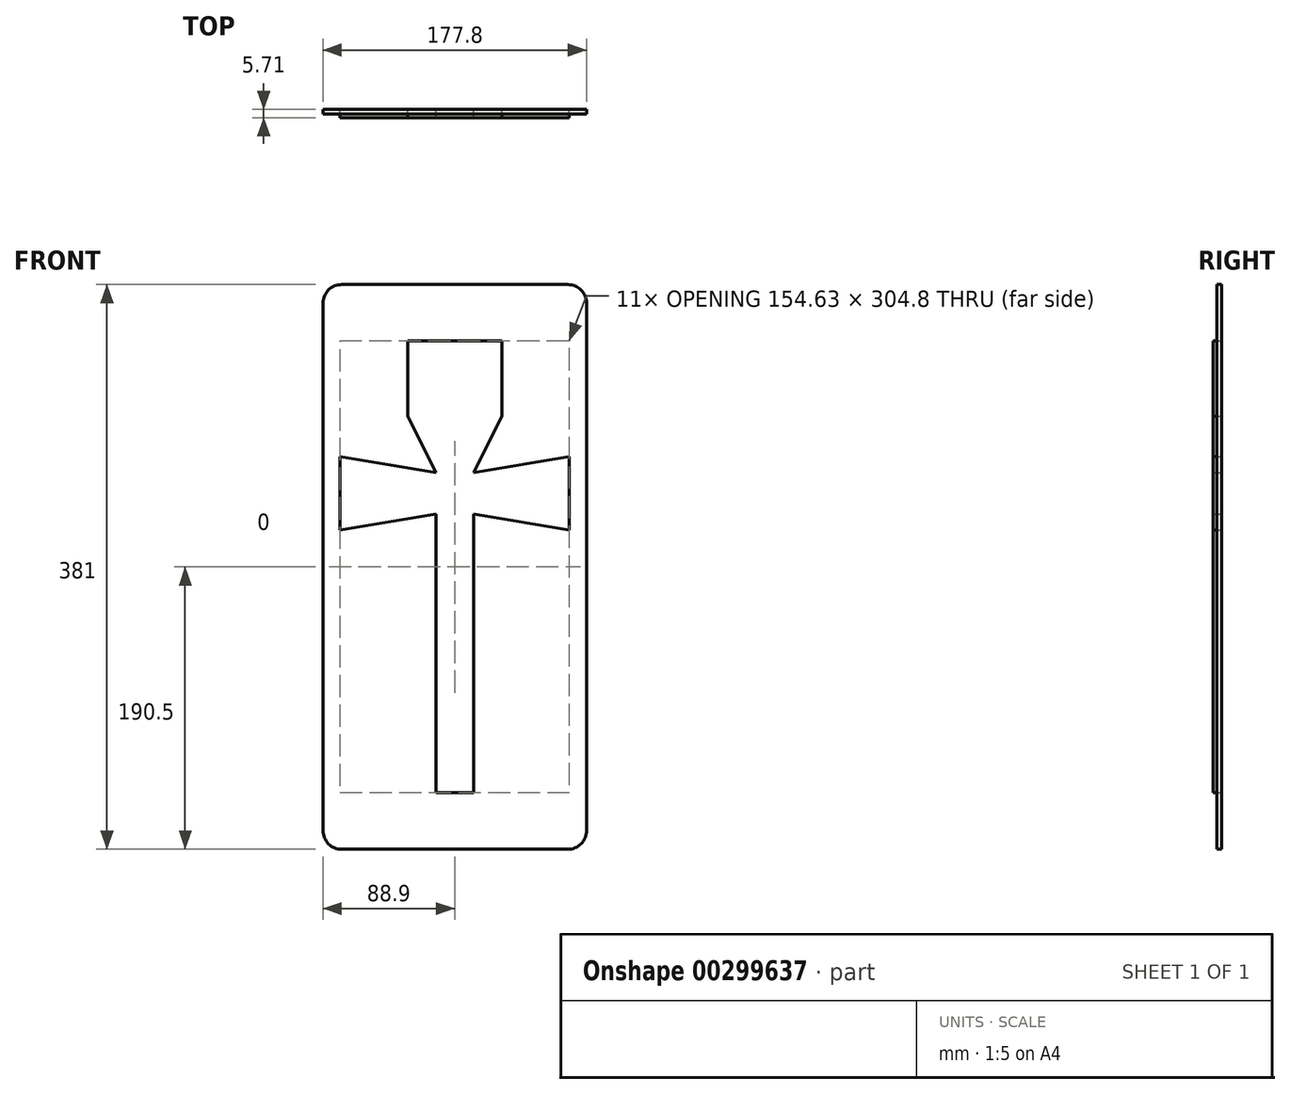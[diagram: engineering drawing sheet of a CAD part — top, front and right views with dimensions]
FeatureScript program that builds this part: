
annotation { "Feature Type Name" : "Feature", "Feature Type Description" : "" }
export const myFeature = defineFeature(function(context is Context, id is Id, definition is map)
    precondition{}
    {
        {
            var Q0;
            Q0=qCreatedBy(makeId("Front.planeOp"),FACE);
            var sketch = newSketch(context, id + "F0", { "sketchPlane" : qUnion([Q0])});
            skLineSegment(sketch, "E0.bottom", {"start": v(-76.2, 190.5) * mm, "end": v(76.2, 190.5) * mm});
            skLineSegment(sketch, "E0.top", {"start": v(-76.2, -190.5) * mm, "end": v(76.2, -190.5) * mm});
            skLineSegment(sketch, "E0.left", {"start": v(-88.9, 177.8) * mm, "end": v(-88.9, -177.8) * mm});
            skLineSegment(sketch, "E0.right", {"start": v(88.9, 177.8) * mm, "end": v(88.9, -177.8) * mm});
            skPoint(sketch, "E0.middle", {"position": v(0, 0) * mm});
            skLineSegment(sketch, "E1.bottom", {"start": v(-12.7, 0) * mm, "end": v(12.7, 0) * mm});
            skLineSegment(sketch, "E1.top", {"start": v(-12.7, -152.4) * mm, "end": v(12.7, -152.4) * mm});
            skLineSegment(sketch, "E1.left", {"start": v(-12.7, 0) * mm, "end": v(-12.7, -152.4) * mm});
            skLineSegment(sketch, "E1.right", {"start": v(12.7, 0) * mm, "end": v(12.7, -152.4) * mm});
            skPoint(sketch, "E1.middle", {"position": v(0, -76.2) * mm});
            skLineSegment(sketch, "E2.top", {"start": v(-12.7, 63.5) * mm, "end": v(12.7, 63.5) * mm});
            skLineSegment(sketch, "E2.left", {"start": v(-12.7, 0) * mm, "end": v(-12.7, 63.5) * mm});
            skLineSegment(sketch, "E2.right", {"start": v(12.7, 0) * mm, "end": v(12.7, 63.5) * mm});
            skPoint(sketch, "E2.middle", {"position": v(0, 31.75) * mm});
            skLineSegment(sketch, "E3", {"start": v(-12.7, 63.5) * mm, "end": v(-31.75, 101.6) * mm});
            skLineSegment(sketch, "E4", {"start": v(-31.75, 101.6) * mm, "end": v(-31.75, 152.4) * mm});
            skLineSegment(sketch, "E5", {"start": v(-31.75, 152.4) * mm, "end": v(31.75, 152.4) * mm});
            skLineSegment(sketch, "E6", {"start": v(31.75, 152.4) * mm, "end": v(31.75, 101.6) * mm});
            skLineSegment(sketch, "E7", {"start": v(31.75, 101.6) * mm, "end": v(12.7, 63.5) * mm});
            skLineSegment(sketch, "E8", {"start": v(-12.7, 63.5) * mm, "end": v(-77.32, 74.28) * mm});
            skLineSegment(sketch, "E9", {"start": v(-77.32, 74.28) * mm, "end": v(-77.32, 24.75) * mm});
            skLineSegment(sketch, "E10", {"start": v(-77.32, 24.75) * mm, "end": v(-12.7, 35.53) * mm});
            skLineSegment(sketch, "E11", {"start": v(12.7, 63.5) * mm, "end": v(77.32, 74.28) * mm});
            skLineSegment(sketch, "E12", {"start": v(77.32, 74.28) * mm, "end": v(77.32, 24.75) * mm});
            skLineSegment(sketch, "E13", {"start": v(77.32, 24.75) * mm, "end": v(12.7, 35.53) * mm});
            skPoint(sketch, "E14.visualSharp", {"position": v(-88.9, 190.5) * mm});
            skArc(sketch, "E14.filletArc", {"start": v(-76.2, 190.5) * mm, "mid": v(-85.18, 186.78) * mm, "end": v(-88.9, 177.8) * mm});
            skPoint(sketch, "E15.visualSharp", {"position": v(88.9, 190.5) * mm});
            skArc(sketch, "E15.filletArc", {"start": v(88.9, 177.8) * mm, "mid": v(85.18, 186.78) * mm, "end": v(76.2, 190.5) * mm});
            skPoint(sketch, "E16.visualSharp", {"position": v(88.9, -190.5) * mm});
            skArc(sketch, "E16.filletArc", {"start": v(76.2, -190.5) * mm, "mid": v(85.18, -186.78) * mm, "end": v(88.9, -177.8) * mm});
            skPoint(sketch, "E17.visualSharp", {"position": v(-88.9, -190.5) * mm});
            skArc(sketch, "E17.filletArc", {"start": v(-88.9, -177.8) * mm, "mid": v(-85.18, -186.78) * mm, "end": v(-76.2, -190.5) * mm});
            skSolve(sketch);
        }
        {
            var Q0;
            Q0 = qSketchRegion(id + "F0", true);
            extrude(context, id + "F1", {"entities" : qUnion([Q0]), "depth" : 3.17 * mm});
        }
        {
            var Q0;
            Q0=makeQuery(id+"F1.opExtrude","CAP_FACE",FACE,{"disambiguationData":[OSD([sQuery(id+"F0.wireOp",EDGE,"E0.bottom"),sQuery(id+"F0.wireOp",EDGE,"E0.top"),sQuery(id+"F0.wireOp",EDGE,"E0.left"),sQuery(id+"F0.wireOp",EDGE,"E0.right")])],"isStart":false});
            var sketch = newSketch(context, id + "F2", { "sketchPlane" : qUnion([Q0])});
            skLineSegment(sketch, "E18.bottom", {"start": v(-12.7, 0) * mm, "end": v(12.7, 0) * mm});
            skLineSegment(sketch, "E18.top", {"start": v(-12.7, -152.4) * mm, "end": v(12.7, -152.4) * mm});
            skLineSegment(sketch, "E18.left", {"start": v(-12.7, 0) * mm, "end": v(-12.7, -152.4) * mm});
            skLineSegment(sketch, "E18.right", {"start": v(12.7, 0) * mm, "end": v(12.7, -152.4) * mm});
            skPoint(sketch, "E18.middle", {"position": v(0, -76.2) * mm});
            skLineSegment(sketch, "E19.top", {"start": v(-12.7, 63.5) * mm, "end": v(12.7, 63.5) * mm});
            skLineSegment(sketch, "E19.left", {"start": v(-12.7, 0) * mm, "end": v(-12.7, 63.5) * mm});
            skLineSegment(sketch, "E19.right", {"start": v(12.7, 0) * mm, "end": v(12.7, 63.5) * mm});
            skPoint(sketch, "E19.middle", {"position": v(0, 31.75) * mm});
            skLineSegment(sketch, "E20", {"start": v(-12.7, 63.5) * mm, "end": v(-31.75, 101.6) * mm});
            skLineSegment(sketch, "E21", {"start": v(-31.75, 101.6) * mm, "end": v(-31.75, 152.4) * mm});
            skLineSegment(sketch, "E22", {"start": v(-31.75, 152.4) * mm, "end": v(31.75, 152.4) * mm});
            skLineSegment(sketch, "E23", {"start": v(31.75, 152.4) * mm, "end": v(31.75, 101.6) * mm});
            skLineSegment(sketch, "E24", {"start": v(31.75, 101.6) * mm, "end": v(12.7, 63.5) * mm});
            skLineSegment(sketch, "E25", {"start": v(-12.7, 63.5) * mm, "end": v(-77.32, 74.28) * mm});
            skLineSegment(sketch, "E26", {"start": v(-77.32, 74.28) * mm, "end": v(-77.32, 24.75) * mm});
            skLineSegment(sketch, "E27", {"start": v(-77.32, 24.75) * mm, "end": v(-12.7, 35.53) * mm});
            skLineSegment(sketch, "E28", {"start": v(12.7, 63.5) * mm, "end": v(77.32, 74.28) * mm});
            skLineSegment(sketch, "E29", {"start": v(77.32, 74.28) * mm, "end": v(77.32, 24.75) * mm});
            skLineSegment(sketch, "E30", {"start": v(77.32, 24.75) * mm, "end": v(12.7, 35.53) * mm});
            skSolve(sketch);
        }
        {
            var Q0;
            Q0 = qSketchRegion(id + "F2", true);
            extrude(context, id + "F3", {"entities" : qUnion([Q0]), "depth" : 2.54 * mm});
        }
    });
